# Revit family: QF_ELECTROLUXPROFESSIONAL_1LSNA3_TE1220E_E
name_source: partatom
category: Attrezzature speciali
units: mm (PartAtom-declared; Revit-internal decimal feet)

## family parameters
Basato su piano di lavoro = No
Condiviso = No
Punto di calcolo locali = No
Quota connettore circolare = Usa diametro
Sempre verticale = Sì
Taglio con vuoti quando caricato = No
Tipo di parte = Normale

## types (3) — shared parameters
Depth = 822 mm
Depth Actual = 822 mm
Height = 850 mm
Height Actual = 1098 mm  [stored 3.60236 ft]
Latent Heat Output = 0.0
Length Actual = 686 mm  [stored 2.25066 ft]
Modello = TE1220E
Phase = 1
Produttore = Electrolux Professional
Sensible Heat Output = 0.0
URL = www.electroluxprofessional.com
Volts = 240 V
Watts = 5000 W
Weight = 70
Width = 686 mm  [stored 2.25066 ft]
zero-valued in all types: Gas KW, Prospetto di default, Steam Pounds per Hour

## per-type parameters (varying)
| type | Cycle | Descrizione | Item Number |
| 988690053 | 50 Hz | myPRO XL SMART PROFESSIONAL TUMBLE DRYER TE1220E 12KG EL 4,8KW VENTED 220-240/50/1N 5KW SYMBOLS SST/DARK BLUE | 1L0GJX |
| 988690055 | 60 Hz | myPRO XL SMART PROFESSIONAL TUMBLE DRYER TE1220E EL 4,8KW VENTED 208-240/60/1 4,8 kW SYMBOLS SST/DARK BLUE | 1L0H21 |
| 988690057 | 50 Hz | TE1220E 230V/50 CN E4,8KW ELX | 1L0GM9 |

note: [stored X ft] marks values corroborated as IEEE doubles in the binary element streams (Revit-internal decimal feet)

## geometry (parser evidence)
native form markers: Sweep x2
no freeform markers — native parametric forms only
